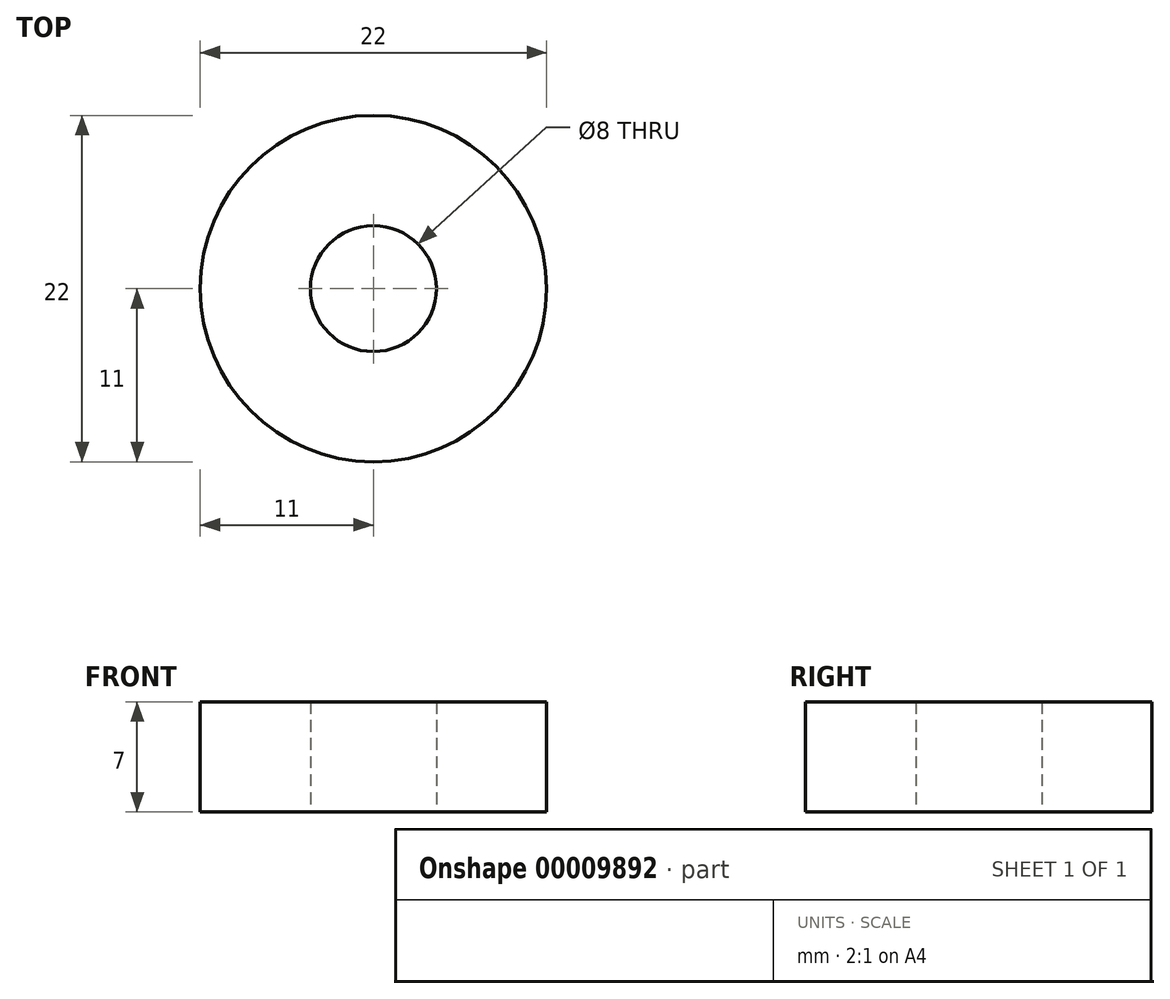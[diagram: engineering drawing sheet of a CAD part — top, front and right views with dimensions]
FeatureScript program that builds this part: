
annotation { "Feature Type Name" : "Feature", "Feature Type Description" : "" }
export const myFeature = defineFeature(function(context is Context, id is Id, definition is map)
    precondition{}
    {
        {
            var Q0;
            Q0=qCreatedBy(makeId("Top.planeOp"),FACE);
            var sketch = newSketch(context, id + "F0", { "sketchPlane" : qUnion([Q0])});
            skCircle(sketch, "E0", {"center": v(0, 0) * mm, "radius": 11 * mm});
            skCircle(sketch, "E1", {"center": v(0, 0) * mm, "radius": 4 * mm});
            skSolve(sketch);
        }
        {
            var Q0;
            Q0 = qSketchRegion(id + "F0", true);
            extrude(context, id + "F1", {"entities" : qUnion([Q0]), "depth" : 7 * mm});
        }
    });
